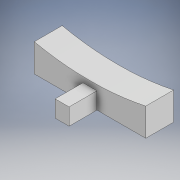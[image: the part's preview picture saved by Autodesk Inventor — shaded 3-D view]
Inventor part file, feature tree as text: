
AUTODESK INVENTOR PART (.ipt)
format: ipt  version: 2020 (Build 240168000, 168)  size: 112,640 bytes
history: native  units: mm
features: extrude x2, sketch x2
ambient origin geometry x8: Origin, YZ Plane, XZ Plane, XY Plane, X Axis, Y Axis, Z Axis, Center Point
bodies: Solide1 (feature_tree)
feature tree (4):
  extrude  "Extrusion1"  Depth=10.0mm
  extrude  "Extrusion2"  Depth=40.0mm
  sketch  "Esquisse1"
  sketch  "Esquisse2"
